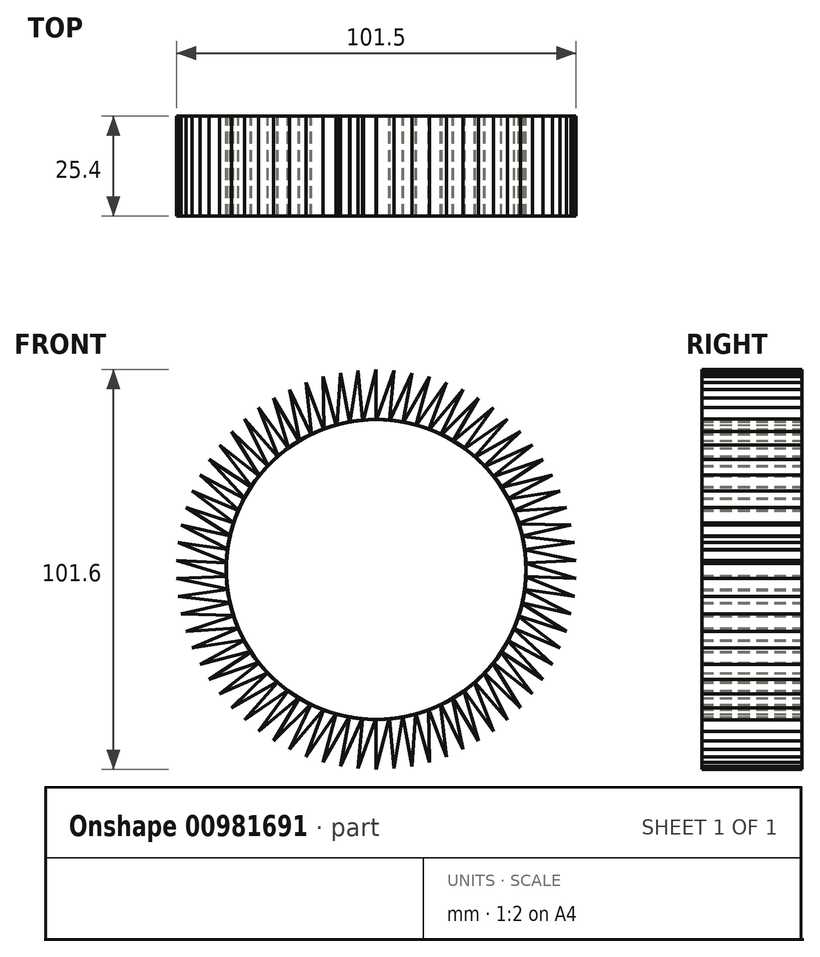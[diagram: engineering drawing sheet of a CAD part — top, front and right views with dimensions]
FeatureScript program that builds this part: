
annotation { "Feature Type Name" : "Feature", "Feature Type Description" : "" }
export const myFeature = defineFeature(function(context is Context, id is Id, definition is map)
    precondition{}
    {
        {
            var Q0;
            Q0=qCreatedBy(makeId("Front.planeOp"),FACE);
            var sketch = newSketch(context, id + "F0", { "sketchPlane" : qUnion([Q0])});
            skCircle(sketch, "E0", {"center": v(0, 0) * mm, "radius": 38.1 * mm});
            skLineSegment(sketch, "E1", {"start": v(0, 38.1) * mm, "end": v(0, 50.8) * mm});
            skLineSegment(sketch, "E2", {"start": v(0, 50.8) * mm, "end": v(-3.26, 37.96) * mm});
            skSolve(sketch);
        }
        {
            var Q0;
            {var subQ0=sQuery(id+"F0.wireOp",EDGE,"E0");var subQ1=makeQuery(id+"F0.imprint","INTERSECT",VERTEX,{"derivedFrom":[subQ0,sQuery(id+"F0.wireOp",EDGE,"E1")]});Q0=makeQuery(id+"F0.imprint","IMPRINT",FACE,{"disambiguationData":[TD([[makeQuery(id+"F0.imprint","IMPRINT",EDGE,{"disambiguationData":[TD([[subQ1,-1.0]])],"derivedFrom":subQ0}),1.0]])]});}
            extrude(context, id + "F1", {"entities" : qUnion([Q0]), "depth" : 25.4 * mm, "offsetDistance" : 25.4 * mm});
        }
        {
            var Q0;
            {var subQ0=sQuery(id+"F0.wireOp",EDGE,"E1");Q0=makeQuery(id+"F0.imprint","IMPRINT",FACE,{"disambiguationData":[TD([[makeQuery(id+"F0.imprint","IMPRINT",EDGE,{"derivedFrom":subQ0}),1.0]])]});}
            extrude(context, id + "F2", {"entities" : qUnion([Q0]), "operationType" : NewBodyOperationType.ADD, "depth" : 25.4 * mm, "offsetDistance" : 25.4 * mm});
        }
        {
            var Q0;
            Q0=makeQuery(id+"F1.opExtrude","SWEPT_BODY",BODY,{"disambiguationData":[OSD([sQuery(id+"F0.wireOp",EDGE,"E0")])]});
            var Q1;
            Q1=makeQuery(id+"F1.opExtrude","SWEPT_FACE",FACE,{"disambiguationData":[OSD([sQuery(id+"F0.wireOp",EDGE,"E0")])]});
            circularPattern(context, id + "F3", {"entities" : qUnion([Q0]), "axis" : qUnion([Q1]), "angle" : 360 * degree, "instanceCount" : 70, "equalSpace" : true});
        }
    });
